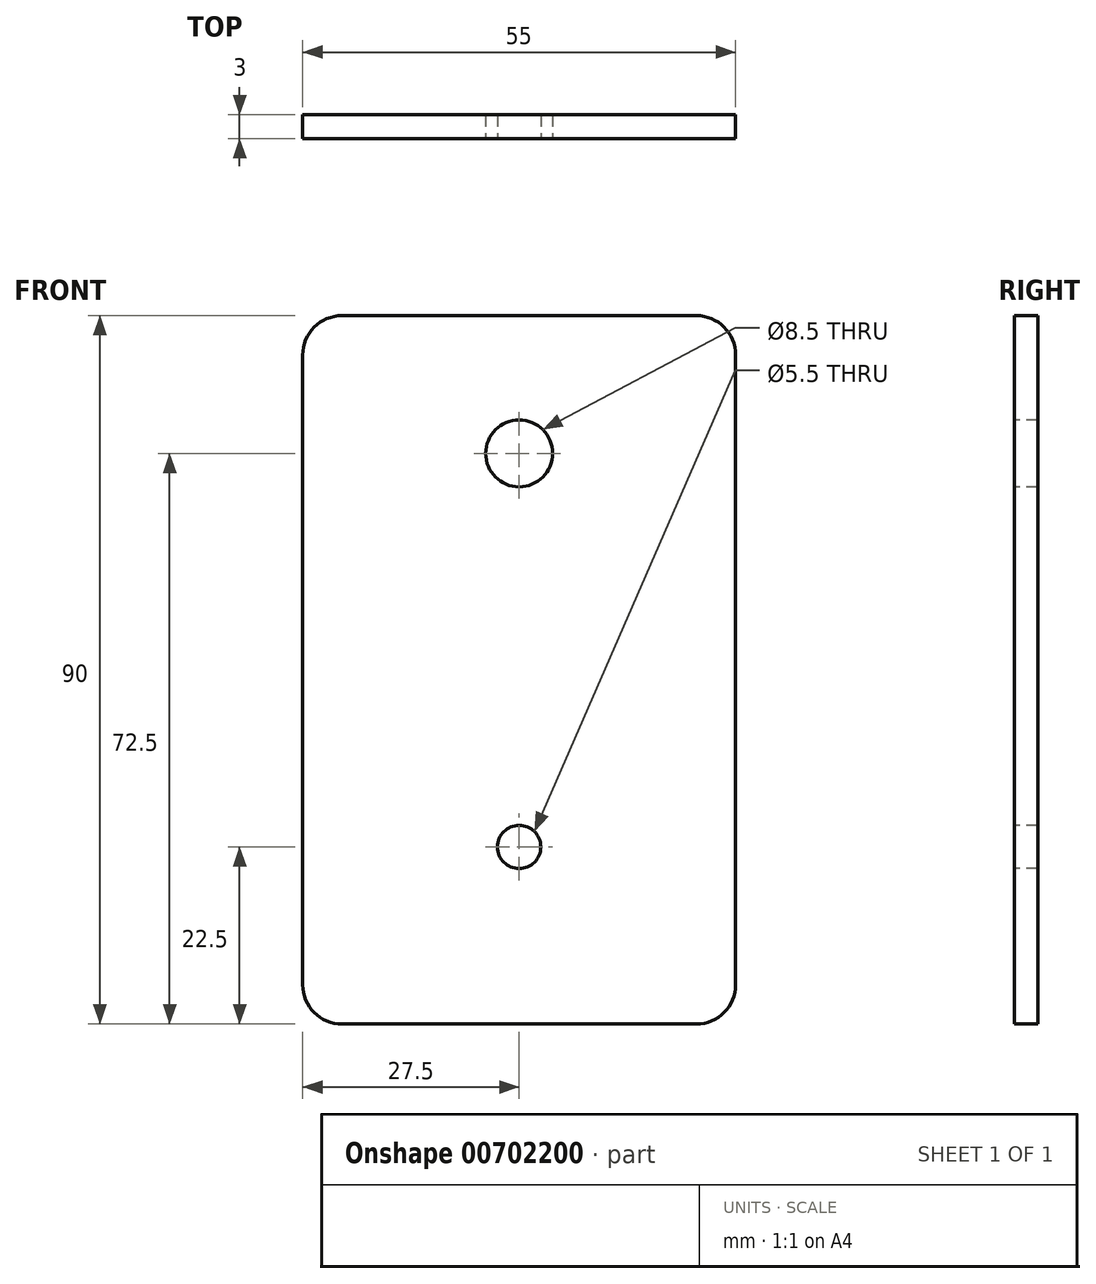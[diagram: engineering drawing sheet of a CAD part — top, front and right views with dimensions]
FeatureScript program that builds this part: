
annotation { "Feature Type Name" : "Feature", "Feature Type Description" : "" }
export const myFeature = defineFeature(function(context is Context, id is Id, definition is map)
    precondition{}
    {
        {
            var Q0;
            Q0=qCreatedBy(makeId("Front.planeOp"),FACE);
            var sketch = newSketch(context, id + "F0", { "sketchPlane" : qUnion([Q0])});
            skLineSegment(sketch, "E0.bottom", {"start": v(27.5, -45) * mm, "end": v(-27.5, -45) * mm});
            skLineSegment(sketch, "E0.top", {"start": v(27.5, 45) * mm, "end": v(-27.5, 45) * mm});
            skLineSegment(sketch, "E0.left", {"start": v(27.5, -45) * mm, "end": v(27.5, 45) * mm});
            skLineSegment(sketch, "E0.right", {"start": v(-27.5, -45) * mm, "end": v(-27.5, 45) * mm});
            skPoint(sketch, "E0.middle", {"position": v(0, 0) * mm});
            skSolve(sketch);
        }
        {
            var Q0;
            Q0=makeQuery(id+"F0.imprint","IMPRINT",FACE,{"disambiguationData":[TD([[makeQuery(id+"F0.imprint","IMPRINT",EDGE,{"derivedFrom":sQuery(id+"F0.wireOp",EDGE,"E0.bottom")}),-1.0]])]});
            extrude(context, id + "F1", {"entities" : qUnion([Q0]), "depth" : 3 * mm, "offsetDistance" : 25 * mm});
        }
        {
            var Q0;
            Q0=makeQuery(id+"F1.opExtrude","CAP_FACE",FACE,{"disambiguationData":[OSD([sQuery(id+"F0.wireOp",EDGE,"E0.bottom"),sQuery(id+"F0.wireOp",EDGE,"E0.top"),sQuery(id+"F0.wireOp",EDGE,"E0.left"),sQuery(id+"F0.wireOp",EDGE,"E0.right")])],"isStart":false});
            var sketch = newSketch(context, id + "F2", { "sketchPlane" : qUnion([Q0])});
            skCircle(sketch, "E1", {"center": v(0, 27.5) * mm, "radius": 4.25 * mm});
            skSolve(sketch);
        }
        {
            var Q0;
            Q0=makeQuery(id+"F2.imprint","IMPRINT",FACE,{"disambiguationData":[TD([[makeQuery(id+"F2.imprint","IMPRINT",EDGE,{"derivedFrom":sQuery(id+"F2.wireOp",EDGE,"E1")}),1.0]])]});
            extrude(context, id + "F3", {"entities" : qUnion([Q0]), "operationType" : NewBodyOperationType.REMOVE, "endBound" : BoundingType.UP_TO_NEXT, "oppositeDirection" : true, "depth" : 25 * mm, "offsetDistance" : 25 * mm});
        }
        {
            var Q0;
            Q0=makeQuery(id+"F1.opExtrude","SWEPT_EDGE",EDGE,{"disambiguationData":[OSD([sQuery(id+"F0.wireOp",EDGE,"E0.top"),sQuery(id+"F0.wireOp",EDGE,"E0.right")])]});
            var Q1;
            Q1=makeQuery(id+"F1.opExtrude","SWEPT_EDGE",EDGE,{"disambiguationData":[OSD([sQuery(id+"F0.wireOp",EDGE,"E0.top"),sQuery(id+"F0.wireOp",EDGE,"E0.left")])]});
            var Q2;
            Q2=makeQuery(id+"F1.opExtrude","SWEPT_EDGE",EDGE,{"disambiguationData":[OSD([sQuery(id+"F0.wireOp",EDGE,"E0.bottom"),sQuery(id+"F0.wireOp",EDGE,"E0.left")])]});
            var Q3;
            Q3=makeQuery(id+"F1.opExtrude","SWEPT_EDGE",EDGE,{"disambiguationData":[OSD([sQuery(id+"F0.wireOp",EDGE,"E0.bottom"),sQuery(id+"F0.wireOp",EDGE,"E0.right")])]});
            fillet(context, id + "F4", {"entities" : qUnion([Q0, Q1, Q2, Q3]), "radius" : 5 * mm, "tangentPropagation" : true, "allowEdgeOverflow" : false});
        }
        {
            var Q0;
            Q0=makeQuery(id+"F1.opExtrude","CAP_FACE",FACE,{"disambiguationData":[OSD([sQuery(id+"F0.wireOp",EDGE,"E0.bottom"),sQuery(id+"F0.wireOp",EDGE,"E0.top"),sQuery(id+"F0.wireOp",EDGE,"E0.left"),sQuery(id+"F0.wireOp",EDGE,"E0.right")])],"isStart":false});
            var sketch = newSketch(context, id + "F5", { "sketchPlane" : qUnion([Q0])});
            skCircle(sketch, "E2", {"center": v(0, -22.5) * mm, "radius": 2.75 * mm});
            skSolve(sketch);
        }
        {
            var Q0;
            Q0=makeQuery(id+"F5.imprint","IMPRINT",FACE,{"disambiguationData":[TD([[makeQuery(id+"F5.imprint","IMPRINT",EDGE,{"derivedFrom":sQuery(id+"F5.wireOp",EDGE,"E2")}),1.0]])]});
            extrude(context, id + "F6", {"entities" : qUnion([Q0]), "operationType" : NewBodyOperationType.REMOVE, "endBound" : BoundingType.UP_TO_NEXT, "oppositeDirection" : true, "depth" : 25 * mm, "offsetDistance" : 25 * mm});
        }
    });
